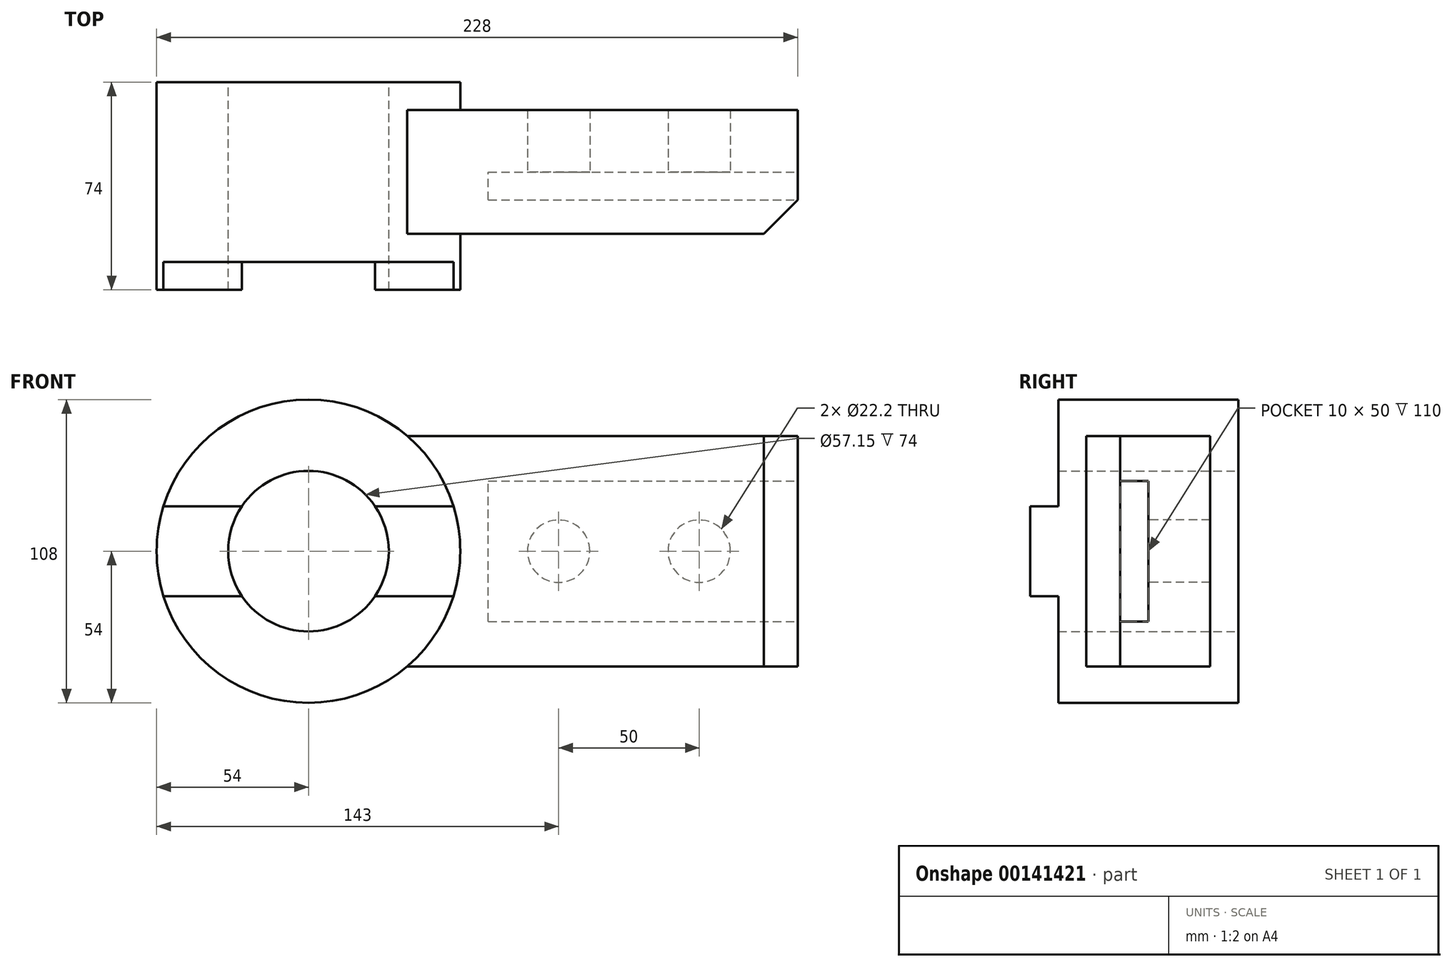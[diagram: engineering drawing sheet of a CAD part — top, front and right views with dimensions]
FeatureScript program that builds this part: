
annotation { "Feature Type Name" : "Feature", "Feature Type Description" : "" }
export const myFeature = defineFeature(function(context is Context, id is Id, definition is map)
    precondition{}
    {
        {
            var Q0;
            Q0=qCreatedBy(makeId("Front.planeOp"),FACE);
            var sketch = newSketch(context, id + "F0", { "sketchPlane" : qUnion([Q0])});
            skCircle(sketch, "E0", {"center": v(0, 0) * mm, "radius": 54 * mm});
            skCircle(sketch, "E1", {"center": v(0, 0) * mm, "radius": 28.57 * mm});
            skLineSegment(sketch, "E2", {"start": v(35.14, 41) * mm, "end": v(174, 41) * mm});
            skLineSegment(sketch, "E3", {"start": v(174, 41) * mm, "end": v(174, -41) * mm});
            skLineSegment(sketch, "E4", {"start": v(174, -41) * mm, "end": v(35.14, -41) * mm});
            skSolve(sketch);
        }
        {
            var Q0;
            Q0=makeQuery(id+"F0.imprint","IMPRINT",FACE,{"disambiguationData":[TD([[makeQuery(id+"F0.imprint","IMPRINT",EDGE,{"derivedFrom":sQuery(id+"F0.wireOp",EDGE,"E1")}),-1.0]])]});
            extrude(context, id + "F1", {"entities" : qUnion([Q0]), "endBound" : BoundingType.SYMMETRIC, "depth" : 64 * mm});
        }
        {
            var Q0;
            {var subQ0=sQuery(id+"F0.wireOp",EDGE,"E2");Q0=makeQuery(id+"F0.imprint","IMPRINT",FACE,{"disambiguationData":[TD([[makeQuery(id+"F0.imprint","IMPRINT",EDGE,{"derivedFrom":subQ0}),-1.0]])]});}
            extrude(context, id + "F2", {"entities" : qUnion([Q0]), "operationType" : NewBodyOperationType.ADD, "endBound" : BoundingType.SYMMETRIC, "depth" : 44 * mm});
        }
        {
            var Q0;
            Q0=makeQuery(id+"F2.opExtrude","SWEPT_FACE",FACE,{"disambiguationData":[OSD([sQuery(id+"F0.wireOp",EDGE,"E2")])]});
            var sketch = newSketch(context, id + "F3", { "sketchPlane" : qUnion([Q0])});
            skLineSegment(sketch, "E5", {"start": v(162, -22) * mm, "end": v(174, -10) * mm});
            skLineSegment(sketch, "E6", {"start": v(162, -22) * mm, "end": v(174, -22) * mm});
            skLineSegment(sketch, "E7", {"start": v(174, -22) * mm, "end": v(174, -10) * mm});
            skSolve(sketch);
        }
        {
            var Q0;
            Q0=makeQuery(id+"F3.imprint","IMPRINT",FACE,{"disambiguationData":[TD([[makeQuery(id+"F3.imprint","IMPRINT",EDGE,{"derivedFrom":sQuery(id+"F3.wireOp",EDGE,"E5")}),-1.0]])]});
            extrude(context, id + "F4", {"entities" : qUnion([Q0]), "operationType" : NewBodyOperationType.REMOVE, "endBound" : BoundingType.THROUGH_ALL, "oppositeDirection" : true, "depth" : 25 * mm});
        }
        {
            var Q0;
            Q0=makeQuery(id+"F2.opExtrude","SWEPT_FACE",FACE,{"disambiguationData":[OSD([sQuery(id+"F0.wireOp",EDGE,"E3")])]});
            var sketch = newSketch(context, id + "F5", { "sketchPlane" : qUnion([Q0])});
            skLineSegment(sketch, "E8.0", {"start": v(-22, -41) * mm, "end": v(-22, 41) * mm});
            skLineSegment(sketch, "E8.1", {"start": v(-10, -41) * mm, "end": v(-10, 41) * mm});
            skLineSegment(sketch, "E9.0", {"start": v(22, 41) * mm, "end": v(22, -41) * mm});
            skLineSegment(sketch, "E10.bottom", {"start": v(-22, 25) * mm, "end": v(0, 25) * mm});
            skLineSegment(sketch, "E10.top", {"start": v(-22, -25) * mm, "end": v(0, -25) * mm});
            skLineSegment(sketch, "E10.left", {"start": v(-22, 25) * mm, "end": v(-22, -25) * mm});
            skLineSegment(sketch, "E10.right", {"start": v(0, 25) * mm, "end": v(0, -25) * mm});
            skSolve(sketch);
        }
        {
            var Q0;
            {var subQ5=sQuery(id+"F5.wireOp",EDGE,"E10.left");Q0=makeQuery(id+"F5.imprint","IMPRINT",FACE,{"disambiguationData":[TD([[makeQuery(id+"F5.imprint","IMPRINT",EDGE,{"derivedFrom":subQ5}),1.0]])]});}
            var Q1;
            {var subQ5=sQuery(id+"F5.wireOp",EDGE,"E10.right");Q1=makeQuery(id+"F5.imprint","IMPRINT",FACE,{"disambiguationData":[TD([[makeQuery(id+"F5.imprint","IMPRINT",EDGE,{"derivedFrom":subQ5}),-1.0]])]});}
            extrude(context, id + "F6", {"entities" : qUnion([Q0, Q1]), "operationType" : NewBodyOperationType.REMOVE, "oppositeDirection" : true, "depth" : 110 * mm});
        }
        {
            var Q0;
            Q0=makeQuery(id+"F1.opExtrude","CAP_FACE",FACE,{"disambiguationData":[OSD([sQuery(id+"F0.wireOp",EDGE,"E0"),sQuery(id+"F0.wireOp",EDGE,"E1")])],"isStart":false});
            var sketch = newSketch(context, id + "F7", { "sketchPlane" : qUnion([Q0])});
            skArc(sketch, "E11", {"start": v(-51.58, 16) * mm, "mid": v(-54, 0) * mm, "end": v(-51.58, -16) * mm});
            skCircle(sketch, "E12.0", {"center": v(0, 0) * mm, "radius": 28.57 * mm});
            skLineSegment(sketch, "E13", {"start": v(-51.58, 16) * mm, "end": v(-23.68, 16) * mm});
            skLineSegment(sketch, "E14", {"start": v(-51.58, -16) * mm, "end": v(-23.68, -16) * mm});
            skArc(sketch, "E15", {"start": v(-23.68, 16) * mm, "mid": v(-28.58, 0) * mm, "end": v(-23.68, -16) * mm});
            skLineSegment(sketch, "E16", {"start": v(23.68, 16) * mm, "end": v(51.58, 16) * mm});
            skLineSegment(sketch, "E17", {"start": v(23.68, -16) * mm, "end": v(51.58, -16) * mm});
            skArc(sketch, "E18", {"start": v(51.58, -16) * mm, "mid": v(54, 0) * mm, "end": v(51.58, 16) * mm});
            skArc(sketch, "E19", {"start": v(23.68, -16) * mm, "mid": v(28.57, 0) * mm, "end": v(23.68, 16) * mm});
            skSolve(sketch);
        }
        {
            var Q0;
            Q0=makeQuery(id+"F7.imprint","IMPRINT",FACE,{"disambiguationData":[TD([[makeQuery(id+"F7.imprint","IMPRINT",EDGE,{"derivedFrom":sQuery(id+"F7.wireOp",EDGE,"E11")}),1.0]])]});
            var Q1;
            {var subQ0=sQuery(id+"F7.wireOp",EDGE,"E16");Q1=makeQuery(id+"F7.imprint","IMPRINT",FACE,{"disambiguationData":[TD([[makeQuery(id+"F7.imprint","IMPRINT",EDGE,{"derivedFrom":subQ0}),-1.0]])]});}
            extrude(context, id + "F8", {"entities" : qUnion([Q0, Q1]), "operationType" : NewBodyOperationType.ADD, "depth" : 10 * mm});
        }
        {
            var Q0;
            {var subQ0=sQuery(id+"F0.wireOp",EDGE,"E2");Q0=makeQuery(id+"F0.imprint","IMPRINT",FACE,{"disambiguationData":[TD([[makeQuery(id+"F0.imprint","IMPRINT",EDGE,{"derivedFrom":subQ0}),-1.0]])]});}
            var sketch = newSketch(context, id + "F9", { "sketchPlane" : qUnion([Q0])});
            skCircle(sketch, "E20", {"center": v(89, 0) * mm, "radius": 11.1 * mm});
            skCircle(sketch, "E21", {"center": v(139, 0) * mm, "radius": 11.1 * mm});
            skSolve(sketch);
        }
        {
            var Q0;
            Q0=makeQuery(id+"F9.imprint","IMPRINT",FACE,{"disambiguationData":[TD([[makeQuery(id+"F9.imprint","IMPRINT",EDGE,{"derivedFrom":sQuery(id+"F9.wireOp",EDGE,"E20")}),1.0]])]});
            var Q1;
            Q1=makeQuery(id+"F9.imprint","IMPRINT",FACE,{"disambiguationData":[TD([[makeQuery(id+"F9.imprint","IMPRINT",EDGE,{"derivedFrom":sQuery(id+"F9.wireOp",EDGE,"E21")}),1.0]])]});
            extrude(context, id + "F10", {"entities" : qUnion([Q0, Q1]), "operationType" : NewBodyOperationType.REMOVE, "endBound" : BoundingType.THROUGH_ALL, "oppositeDirection" : true, "depth" : 25 * mm});
        }
    });
